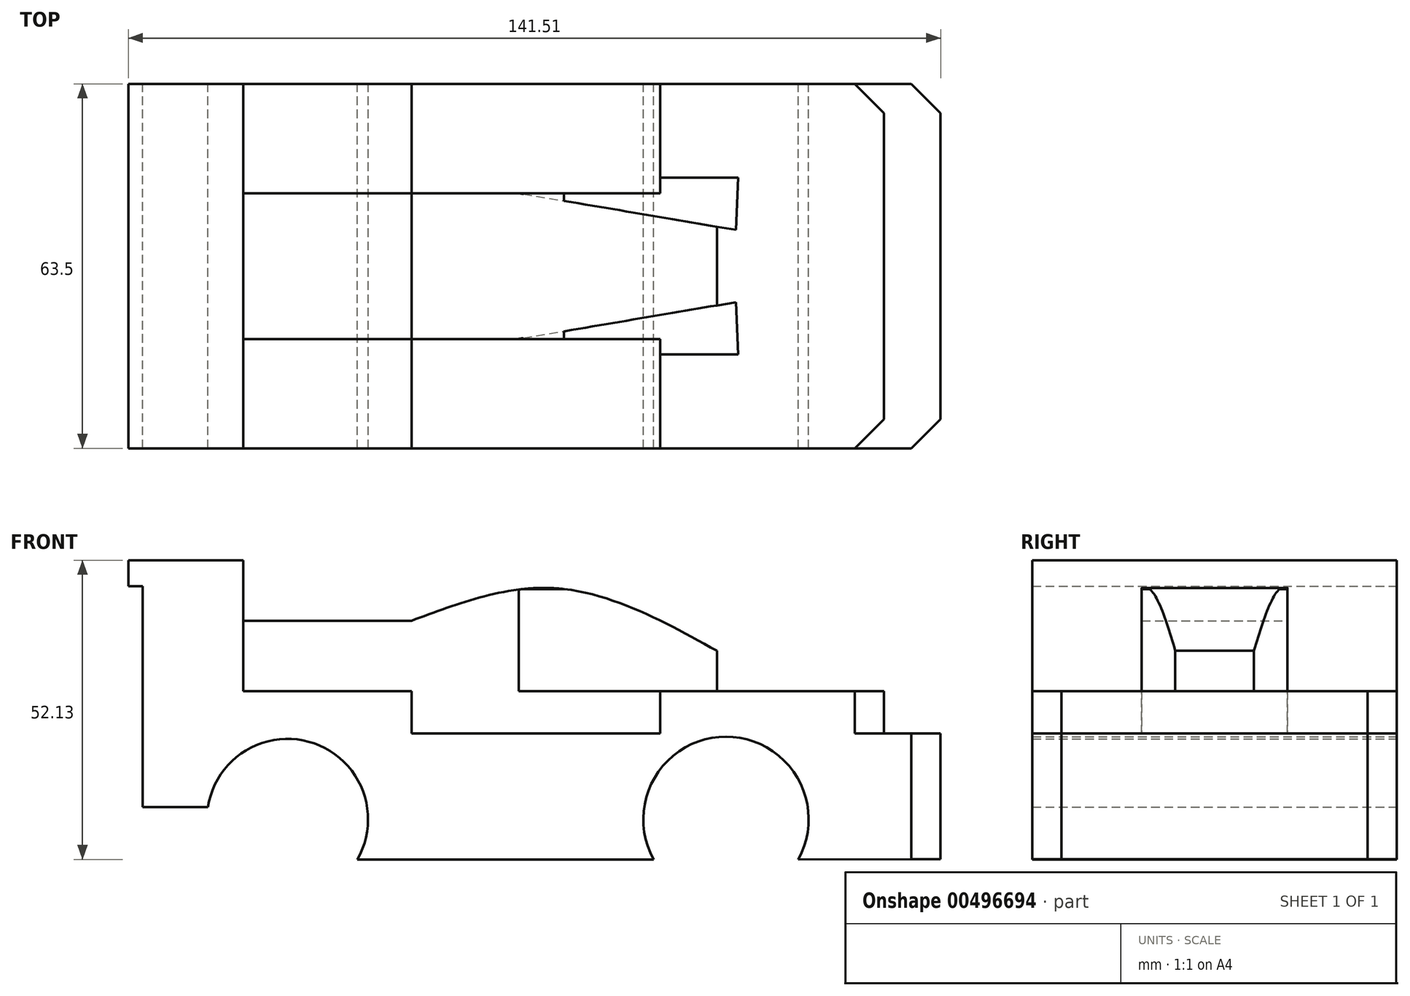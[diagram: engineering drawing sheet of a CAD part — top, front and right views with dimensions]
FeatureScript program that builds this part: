
annotation { "Feature Type Name" : "Feature", "Feature Type Description" : "" }
export const myFeature = defineFeature(function(context is Context, id is Id, definition is map)
    precondition{}
    {
        {
            var Q0;
            Q0=qCreatedBy(makeId("Front.planeOp"),FACE);
            var sketch = newSketch(context, id + "F0", { "sketchPlane" : qUnion([Q0])});
            skLineSegment(sketch, "E0", {"start": v(-54.75, 5.02) * mm, "end": v(-54.75, -37.98) * mm});
            skLineSegment(sketch, "E1", {"start": v(-54.75, 5.02) * mm, "end": v(-37.22, 5.02) * mm});
            skLineSegment(sketch, "E2", {"start": v(-37.22, 5.02) * mm, "end": v(-37.22, -17.77) * mm});
            skLineSegment(sketch, "E3", {"start": v(-37.22, -17.77) * mm, "end": v(-7.88, -17.77) * mm});
            skLineSegment(sketch, "E4", {"start": v(-7.88, -17.77) * mm, "end": v(-7.88, -25.18) * mm});
            skLineSegment(sketch, "E5", {"start": v(-7.88, -25.18) * mm, "end": v(35.44, -25.18) * mm});
            skLineSegment(sketch, "E6", {"start": v(35.44, -25.18) * mm, "end": v(35.44, -17.77) * mm});
            skLineSegment(sketch, "E7", {"start": v(35.44, -17.77) * mm, "end": v(74.43, -17.77) * mm});
            skLineSegment(sketch, "E8", {"start": v(74.43, -17.77) * mm, "end": v(74.43, -25.18) * mm});
            skLineSegment(sketch, "E9", {"start": v(74.43, -25.18) * mm, "end": v(84.32, -25.18) * mm});
            skLineSegment(sketch, "E10", {"start": v(84.32, -25.18) * mm, "end": v(84.32, -47.08) * mm});
            skLineSegment(sketch, "E11.bottom", {"start": v(-37.22, -5.53) * mm, "end": v(-7.88, -5.53) * mm});
            skLineSegment(sketch, "E11.left", {"start": v(-37.22, -5.53) * mm, "end": v(-37.22, -17.77) * mm});
            skLineSegment(sketch, "E11.right", {"start": v(-7.88, -5.53) * mm, "end": v(-7.88, -17.77) * mm});
            skLineSegment(sketch, "E12.left", {"start": v(-7.88, -14.76) * mm, "end": v(-7.88, -17.77) * mm});
            skLineSegment(sketch, "E12.right", {"start": v(35.44, -17.77) * mm, "end": v(35.44, -17.77) * mm});
            skCircle(sketch, "E13", {"center": v(-29.47, -40.14) * mm, "radius": 14.03 * mm});
            skCircle(sketch, "E14", {"center": v(46.92, -40.14) * mm, "radius": 14.4 * mm});
            skLineSegment(sketch, "E15", {"start": v(-17.3, -47.11) * mm, "end": v(34.31, -47.11) * mm});
            skLineSegment(sketch, "E16.bottom", {"start": v(-54.75, 5.02) * mm, "end": v(-57.2, 5.02) * mm});
            skLineSegment(sketch, "E16.top", {"start": v(-54.75, 0.52) * mm, "end": v(-57.2, 0.52) * mm});
            skLineSegment(sketch, "E16.left", {"start": v(-54.75, 5.02) * mm, "end": v(-54.75, 0.52) * mm});
            skLineSegment(sketch, "E16.right", {"start": v(-57.2, 5.02) * mm, "end": v(-57.2, 0.52) * mm});
            skLineSegment(sketch, "E17", {"start": v(59.53, -47.11) * mm, "end": v(84.32, -47.08) * mm});
            skLineSegment(sketch, "E18", {"start": v(-54.75, -37.98) * mm, "end": v(-43.34, -37.98) * mm});
            skFitSpline(sketch, "E19", {"points": [v(-7.88, -5.53) * mm, v(18.7, 0) * mm, v(45.34, -10.77) * mm], "startDerivative": vector(48.15, 17.54) * mm, "endDerivative": vector(36.89, -20.3) * mm});
            skLineSegment(sketch, "E20", {"start": v(45.34, -10.77) * mm, "end": v(45.34, -17.77) * mm});
            skSolve(sketch);
        }
        {
            var Q0;
            Q0=makeQuery(id+"F0.imprint","IMPRINT",FACE,{"disambiguationData":[TD([[makeQuery(id+"F0.imprint","IMPRINT",EDGE,{"derivedFrom":sQuery(id+"F0.wireOp",EDGE,"E0")}),1.0]])]});
            extrude(context, id + "F1", {"entities" : qUnion([Q0]), "endBound" : BoundingType.SYMMETRIC, "depth" : 63.5 * mm});
        }
        {
            var Q0;
            Q0=makeQuery(id+"F0.imprint","IMPRINT",FACE,{"disambiguationData":[TD([[makeQuery(id+"F0.imprint","IMPRINT",EDGE,{"derivedFrom":sQuery(id+"F0.wireOp",EDGE,"E4")}),1.0]])]});
            extrude(context, id + "F2", {"entities" : qUnion([Q0]), "operationType" : NewBodyOperationType.ADD, "endBound" : BoundingType.SYMMETRIC, "depth" : 25.4 * mm});
        }
        {
            var Q0;
            Q0=makeQuery(id+"F0.imprint","IMPRINT",FACE,{"disambiguationData":[TD([[makeQuery(id+"F0.imprint","IMPRINT",EDGE,{"derivedFrom":sQuery(id+"F0.wireOp",EDGE,"E11.bottom")}),-1.0]])]});
            extrude(context, id + "F3", {"entities" : qUnion([Q0]), "operationType" : NewBodyOperationType.ADD, "endBound" : BoundingType.SYMMETRIC, "depth" : 25.4 * mm});
        }
        {
            var Q0;
            Q0=makeQuery(id+"F0.imprint","IMPRINT",FACE,{"disambiguationData":[TD([[makeQuery(id+"F0.imprint","IMPRINT",EDGE,{"derivedFrom":sQuery(id+"F0.wireOp",EDGE,"E16.bottom")}),1.0]])]});
            extrude(context, id + "F4", {"entities" : qUnion([Q0]), "operationType" : NewBodyOperationType.ADD, "endBound" : BoundingType.SYMMETRIC, "depth" : 63.5 * mm});
        }
        {
            var Q0;
            Q0=makeQuery(id+"F1.opExtrude","CAP_EDGE",EDGE,{"disambiguationData":[OSD([sQuery(id+"F0.wireOp",EDGE,"E8")])],"isStart":false});
            var Q1;
            Q1=makeQuery(id+"F1.opExtrude","CAP_EDGE",EDGE,{"disambiguationData":[OSD([sQuery(id+"F0.wireOp",EDGE,"E8")])],"isStart":true});
            var Q2;
            Q2=makeQuery(id+"F1.opExtrude","CAP_EDGE",EDGE,{"disambiguationData":[OSD([sQuery(id+"F0.wireOp",EDGE,"E10")])],"isStart":true});
            var Q3;
            Q3=makeQuery(id+"F1.opExtrude","CAP_EDGE",EDGE,{"disambiguationData":[OSD([sQuery(id+"F0.wireOp",EDGE,"E10")])],"isStart":false});
            chamfer(context, id + "F5", {"entities" : qUnion([Q0, Q1, Q2, Q3]), "width" : 5.08 * mm, "tangentPropagation" : true});
        }
        {
            var Q0;
            Q0=qCreatedBy(makeId("Top.planeOp"),FACE);
            var sketch = newSketch(context, id + "F6", { "sketchPlane" : qUnion([Q0])});
            skLineSegment(sketch, "E21.bottom", {"start": v(7.54, -15.41) * mm, "end": v(49.02, -15.38) * mm});
            skLineSegment(sketch, "E21.top", {"start": v(7.45, -13.27) * mm, "end": v(48.66, -6.3) * mm});
            skLineSegment(sketch, "E21.left", {"start": v(7.54, -15.41) * mm, "end": v(7.45, -13.27) * mm});
            skLineSegment(sketch, "E21.right", {"start": v(49.02, -15.38) * mm, "end": v(48.66, -6.3) * mm});
            skLineSegment(sketch, "E22.MirrorCS", {"start": v(49.02, 15.38) * mm, "end": v(48.66, 6.3) * mm});
            skLineSegment(sketch, "E23.MirrorCS", {"start": v(7.54, 15.41) * mm, "end": v(49.02, 15.38) * mm});
            skLineSegment(sketch, "E24.MirrorCS", {"start": v(7.45, 13.27) * mm, "end": v(48.66, 6.3) * mm});
            skLineSegment(sketch, "E25.MirrorCS", {"start": v(7.54, 15.41) * mm, "end": v(7.45, 13.27) * mm});
            skSolve(sketch);
        }
        {
            var Q0;
            Q0 = qSketchRegion(id + "F6", true);
            extrude(context, id + "F7", {"entities" : qUnion([Q0]), "operationType" : NewBodyOperationType.REMOVE, "oppositeDirection" : true, "depth" : 17.78 * mm});
        }
    });
